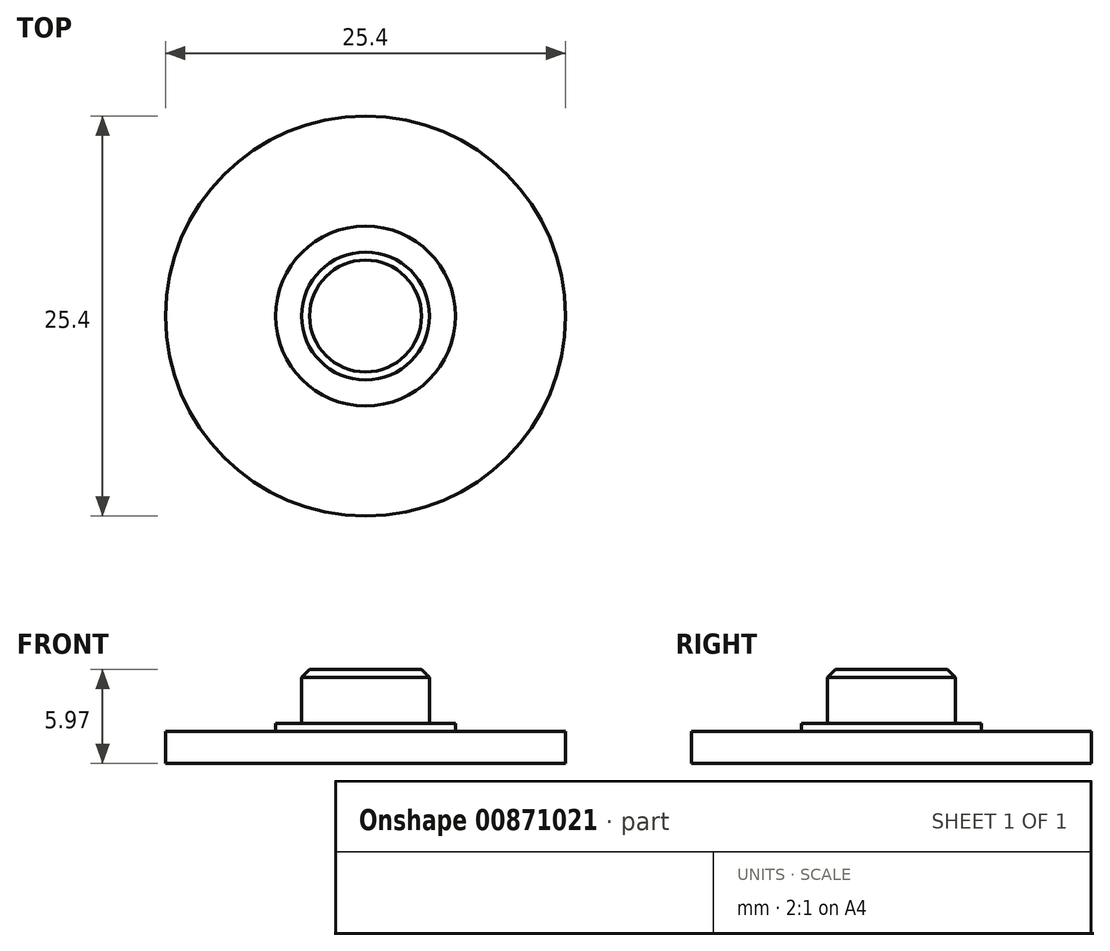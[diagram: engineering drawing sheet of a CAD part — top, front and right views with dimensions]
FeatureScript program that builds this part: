
annotation { "Feature Type Name" : "Feature", "Feature Type Description" : "" }
export const myFeature = defineFeature(function(context is Context, id is Id, definition is map)
    precondition{}
    {
        {
            var Q0;
            Q0=qCreatedBy(makeId("Top.planeOp"),FACE);
            var sketch = newSketch(context, id + "F0", { "sketchPlane" : qUnion([Q0])});
            skCircle(sketch, "E0", {"center": v(0, 0) * mm, "radius": 12.7 * mm});
            skSolve(sketch);
        }
        {
            var Q0;
            Q0=makeQuery(id+"F0.imprint","IMPRINT",FACE,{"disambiguationData":[TD([[makeQuery(id+"F0.imprint","IMPRINT",EDGE,{"derivedFrom":sQuery(id+"F0.wireOp",EDGE,"E0")}),1.0]])]});
            extrude(context, id + "F1", {"entities" : qUnion([Q0]), "depth" : 2.03 * mm, "offsetDistance" : 25.4 * mm});
        }
        {
            var Q0;
            Q0=qCreatedBy(makeId("Top.planeOp"),FACE);
            var sketch = newSketch(context, id + "F2", { "sketchPlane" : qUnion([Q0])});
            skCircle(sketch, "E1", {"center": v(0, 0) * mm, "radius": 4.06 * mm});
            skSolve(sketch);
        }
        {
            var Q0;
            Q0 = qSketchRegion(id + "F2", true);
            extrude(context, id + "F3", {"entities" : qUnion([Q0]), "operationType" : NewBodyOperationType.ADD, "depth" : 5.97 * mm, "offsetDistance" : 25.4 * mm});
        }
        {
            var Q0;
            Q0=makeQuery(id+"F3.opExtrude","CAP_EDGE",EDGE,{"disambiguationData":[OSD([sQuery(id+"F2.wireOp",EDGE,"E1")])],"isStart":false});
            chamfer(context, id + "F4", {"entities" : qUnion([Q0]), "width" : 0.5 * mm, "tangentPropagation" : true});
        }
        {
            var Q0;
            Q0=qCreatedBy(makeId("Top.planeOp"),FACE);
            var sketch = newSketch(context, id + "F5", { "sketchPlane" : qUnion([Q0])});
            skCircle(sketch, "E2", {"center": v(0, 0) * mm, "radius": 5.72 * mm});
            skSolve(sketch);
        }
        {
            var Q0;
            Q0 = qSketchRegion(id + "F5", true);
            extrude(context, id + "F6", {"entities" : qUnion([Q0]), "operationType" : NewBodyOperationType.ADD, "depth" : 2.54 * mm, "offsetDistance" : 25.4 * mm});
        }
    });
